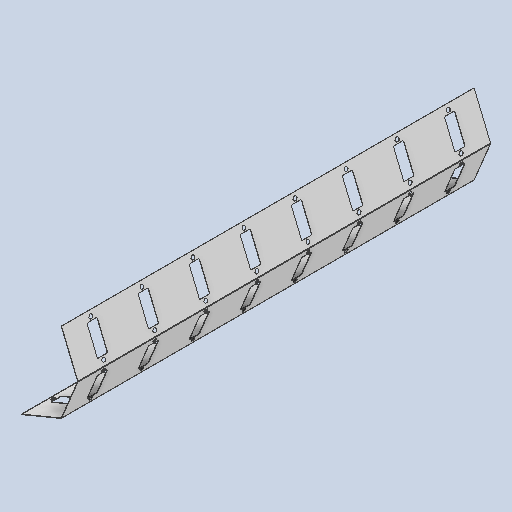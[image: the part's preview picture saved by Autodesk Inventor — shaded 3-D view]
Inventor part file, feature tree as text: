
AUTODESK INVENTOR PART (.ipt)
format: ipt  version: 2025 (Build 290162010, 162A)  size: 929,792 bytes
history: native  units: mm
features: sheet_metal_op x3, other x3, sketch x2, extrude x1, fillet x1, pattern_circular x1, pattern_linear x1
ambient origin geometry x8: Origin, YZ Plane, XZ Plane, XY Plane, X Axis, Y Axis, Z Axis, Center Point
bodies: Body1 (feature_tree)
feature tree (12):
  sheet_metal_op  "Contour Flange2"
  extrude  "Extrusion4"  Depth=2.0mm
  fillet  "Fillet1"  Radius=1.0mm
  pattern_circular  "Circular Pattern1"  [2 undecoded]
  pattern_linear  "Rectangular Pattern2"  Count1=202  [1 undecoded]
  other  "Corner Chamfer1"
  sketch  "Sketch2"  dims[d25=2.0mm d26=2.0mm d27=1.0mm]
  other  "Plate2"
  sheet_metal_op  "Bend2"
  sheet_metal_op  "Corner2"
  sketch  "Sketch10"  dims[d28=4.0mm d29=2.0mm d30=2020.0mm d31=2.0mm d32=3.0mm d33=8.0mm d34=2.0mm d35=2.0mm d56=513.0mm d58=4.0mm d69=0.9mm d70=4.0mm d71=0.9mm d107=135.0mm d108=50.0mm d112=0.0mm d113=0.0mm d114=5.0mm d115=30.0mm d116=90.0deg d118=125.0mm d119=80.0mm d121=250.0mm d122=2.0mm d123=6.0mm d124=45.0deg d125=165.0mm d126=16.8mm d127=16.8mm]
  other  "Definition1"
note: 3 required parameter values undecoded (feature->parameter linkage not recoverable at this tier; creation-order binding heuristic only, values carry confidence <= 0.55)
